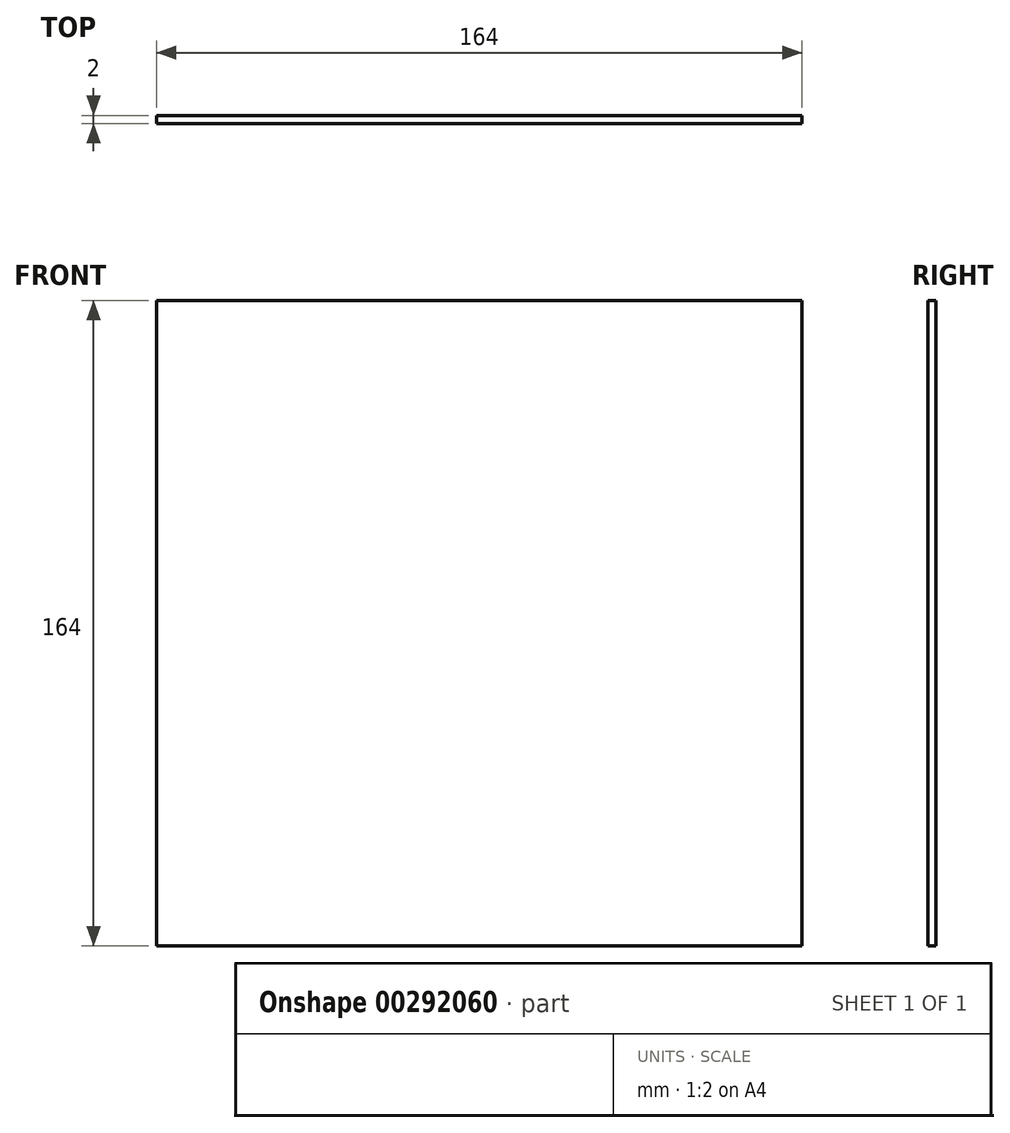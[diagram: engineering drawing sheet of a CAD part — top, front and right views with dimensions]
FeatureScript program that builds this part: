
annotation { "Feature Type Name" : "Feature", "Feature Type Description" : "" }
export const myFeature = defineFeature(function(context is Context, id is Id, definition is map)
    precondition{}
    {
        {
            var Q0;
            Q0=qCreatedBy(makeId("Front.planeOp"),FACE);
            var sketch = newSketch(context, id + "F0", { "sketchPlane" : qUnion([Q0])});
            skLineSegment(sketch, "E0.bottom", {"start": v(82, -82) * mm, "end": v(-82, -82) * mm});
            skLineSegment(sketch, "E0.top", {"start": v(82, 82) * mm, "end": v(-82, 82) * mm});
            skLineSegment(sketch, "E0.left", {"start": v(82, -82) * mm, "end": v(82, 82) * mm});
            skLineSegment(sketch, "E0.right", {"start": v(-82, -82) * mm, "end": v(-82, 82) * mm});
            skPoint(sketch, "E0.middle", {"position": v(0, 0) * mm});
            skSolve(sketch);
        }
        {
            var Q0;
            Q0=makeQuery(id+"F0.imprint","IMPRINT",FACE,{"disambiguationData":[TD([[makeQuery(id+"F0.imprint","IMPRINT",EDGE,{"derivedFrom":sQuery(id+"F0.wireOp",EDGE,"E0.bottom")}),-1.0]])]});
            extrude(context, id + "F1", {"entities" : qUnion([Q0]), "depth" : 2 * mm});
        }
    });
